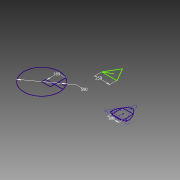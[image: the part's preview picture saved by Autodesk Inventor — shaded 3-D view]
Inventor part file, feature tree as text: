
AUTODESK INVENTOR PART (.ipt)
format: ipt  version: 2013 (Build 170138000, 138)  size: 69,632 bytes
history: native  units: mm
features: sketch x1
ambient origin geometry x8: Origin, YZ Plane, XZ Plane, XY Plane, X Axis, Y Axis, Z Axis, Center Point
feature tree (1):
  sketch  "Sketch1"  dims[d2=590.0mm d3=250.0mm d4=189.0mm d9=180.0mm]
